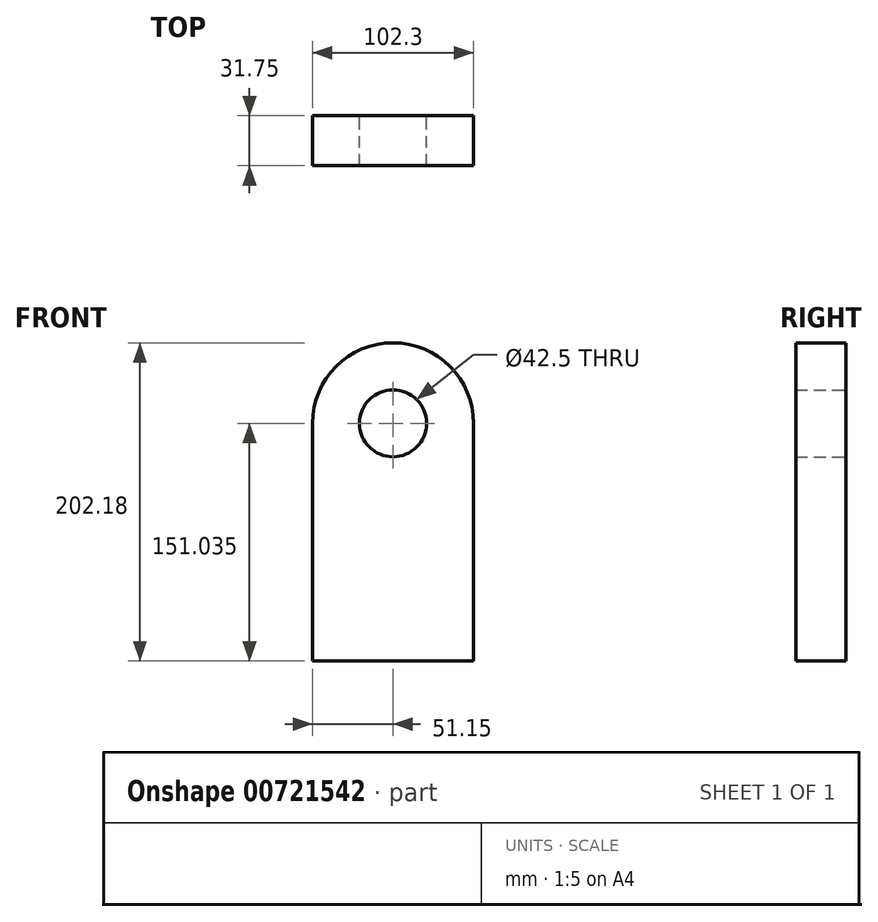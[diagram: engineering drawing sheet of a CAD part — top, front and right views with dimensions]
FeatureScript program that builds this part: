
annotation { "Feature Type Name" : "Feature", "Feature Type Description" : "" }
export const myFeature = defineFeature(function(context is Context, id is Id, definition is map)
    precondition{}
    {
        {
            var Q0;
            Q0=qCreatedBy(makeId("Front.planeOp"),FACE);
            var sketch = newSketch(context, id + "F0", { "sketchPlane" : qUnion([Q0])});
            skLineSegment(sketch, "E0.bottom", {"start": v(51.15, 75.52) * mm, "end": v(-51.15, 75.52) * mm});
            skLineSegment(sketch, "E0.top", {"start": v(51.15, -75.52) * mm, "end": v(-51.15, -75.52) * mm});
            skLineSegment(sketch, "E0.left", {"start": v(51.15, 75.52) * mm, "end": v(51.15, -75.52) * mm});
            skLineSegment(sketch, "E0.right", {"start": v(-51.15, 75.52) * mm, "end": v(-51.15, -75.52) * mm});
            skPoint(sketch, "E0.middle", {"position": v(0, 0) * mm});
            skArc(sketch, "E1", {"start": v(51.15, 75.52) * mm, "mid": v(0, 126.66) * mm, "end": v(-51.15, 75.52) * mm});
            skCircle(sketch, "E2", {"center": v(0, 75.52) * mm, "radius": 21.25 * mm});
            skSolve(sketch);
        }
        {
            var Q0;
            {var subQ0=sQuery(id+"F0.wireOp",EDGE,"E1");Q0=makeQuery(id+"F0.imprint","IMPRINT",FACE,{"disambiguationData":[TD([[makeQuery(id+"F0.imprint","IMPRINT",EDGE,{"derivedFrom":subQ0}),1.0]])]});}
            var Q1;
            Q1=makeQuery(id+"F0.imprint","IMPRINT",FACE,{"disambiguationData":[TD([[makeQuery(id+"F0.imprint","IMPRINT",EDGE,{"derivedFrom":sQuery(id+"F0.wireOp",EDGE,"E0.top")}),-1.0]])]});
            extrude(context, id + "F1", {"entities" : qUnion([Q0, Q1]), "depth" : 31.75 * mm, "offsetDistance" : 25.4 * mm});
        }
    });
